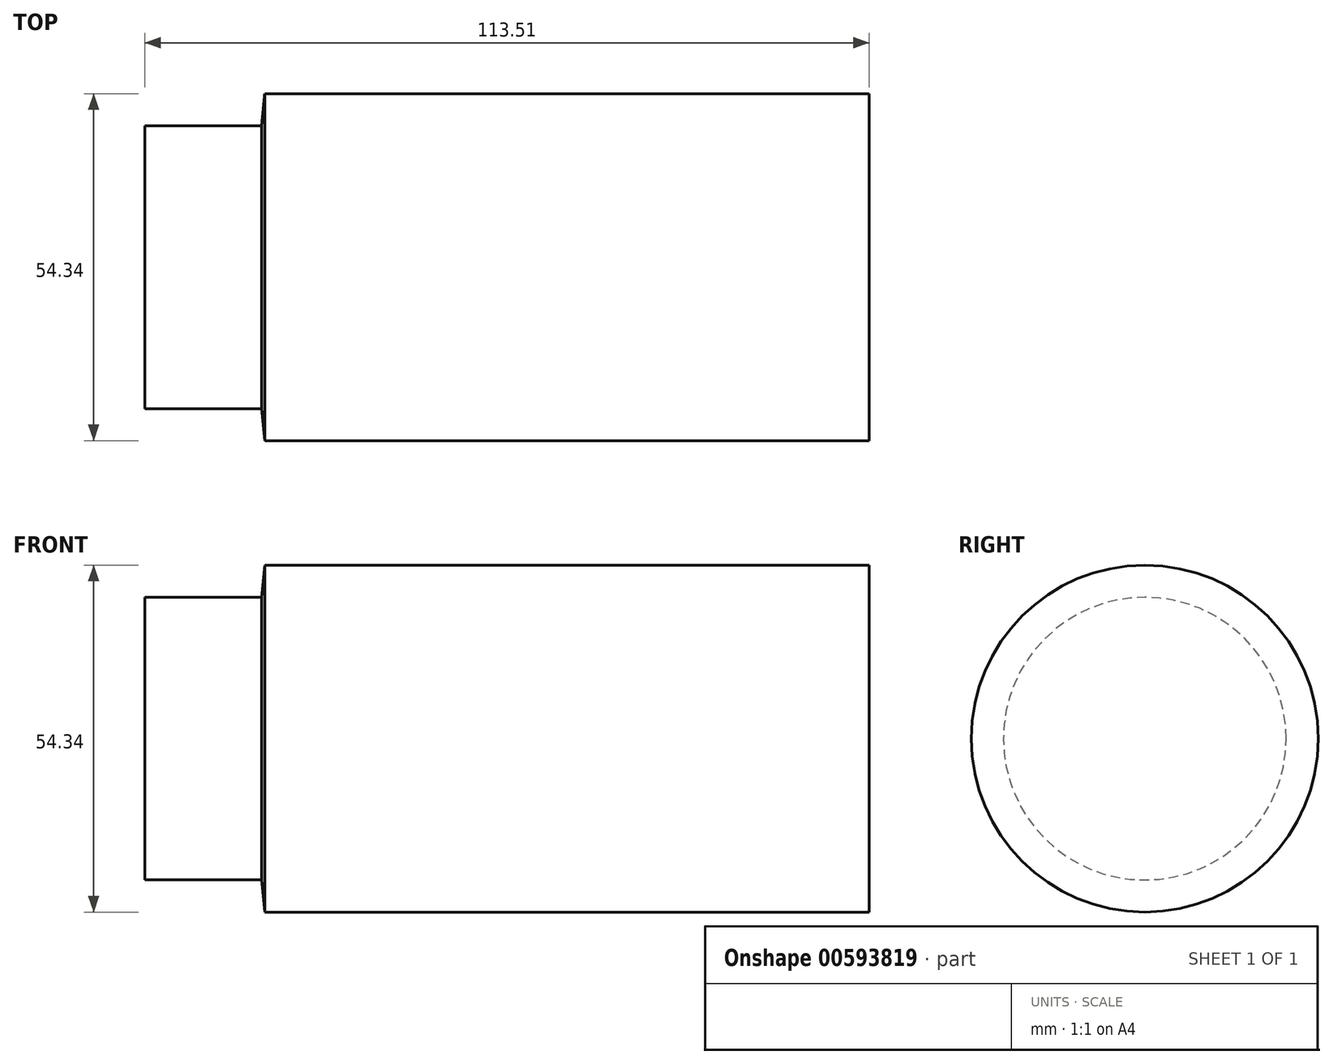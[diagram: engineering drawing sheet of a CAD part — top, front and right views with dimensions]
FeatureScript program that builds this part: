
annotation { "Feature Type Name" : "Feature", "Feature Type Description" : "" }
export const myFeature = defineFeature(function(context is Context, id is Id, definition is map)
    precondition{}
    {
        {
            var Q0;
            Q0=qCreatedBy(makeId("Top.planeOp"),FACE);
            var sketch = newSketch(context, id + "F0", { "sketchPlane" : qUnion([Q0])});
            skLineSegment(sketch, "E0", {"start": v(-48.96, -44.1) * mm, "end": v(45.74, -44.1) * mm});
            skLineSegment(sketch, "E1", {"start": v(45.74, -44.1) * mm, "end": v(45.74, -16.94) * mm});
            skLineSegment(sketch, "E2", {"start": v(45.74, -16.94) * mm, "end": v(-67.77, -16.94) * mm});
            skLineSegment(sketch, "E3", {"start": v(-67.77, -16.94) * mm, "end": v(-67.77, -39.08) * mm});
            skLineSegment(sketch, "E4", {"start": v(-67.77, -39.08) * mm, "end": v(-49.46, -39.08) * mm});
            skLineSegment(sketch, "E5", {"start": v(-49.46, -39.08) * mm, "end": v(-48.96, -44.1) * mm});
            skSolve(sketch);
        }
        {
            var Q0;
            Q0=makeQuery(id+"F0.imprint","IMPRINT",FACE,{"disambiguationData":[TD([[makeQuery(id+"F0.imprint","IMPRINT",EDGE,{"derivedFrom":sQuery(id+"F0.wireOp",EDGE,"E0")}),1.0]])]});
            var Q1;
            Q1=sQuery(id+"F0.wireOp",EDGE,"E2");
            revolve(context, id + "F1", {"entities" : qUnion([Q0]), "axis" : qUnion([Q1]), "revolveType" : RevolveType.FULL});
        }
    });
